# Revit family: Daloc S30 snabbsortiment
name_source: partatom
category: Doors
revit_build: Autodesk Revit LT 2017 (Build: 20160225_1515(x64)
units: mm (PartAtom-declared; Revit-internal decimal feet)

## family parameters
Always vertical = Yes
Cut with Voids When Loaded = No
Host = Wall
OmniClass Number = 23.30.10.00
OmniClass Title = Doors
Room Calculation Point = No
Shared = No

## types (4) — shared parameters
Frame Projection Ext. = 25 mm  [stored 0.082021 ft]
Frame Projection Int. = 25 mm  [stored 0.082021 ft]
Frame Width = 75 mm
Function = Interior
Wall Closure = By host

## per-type parameters (varying)
| type | Height | Modulbredd | Modulhöjd | Width |
| 9x21 | 2100 mm | 9 | 21 | 900 mm  [stored 2.95276 ft] |
| 10x21 | 2100 mm | 10 | 21 | 1000 mm  [stored 3.28084 ft] |
| 9x20 | 2000 mm  [stored 6.56168 ft] | 9 | 20 | 900 mm  [stored 2.95276 ft] |
| 10x20 | 2000 mm  [stored 6.56168 ft] | 10 | 20 | 1000 mm  [stored 3.28084 ft] |

note: [stored X ft] marks values corroborated as IEEE doubles in the binary element streams (Revit-internal decimal feet)

## geometry (parser evidence)
native form markers: Sweep x16
no freeform markers — native parametric forms only
